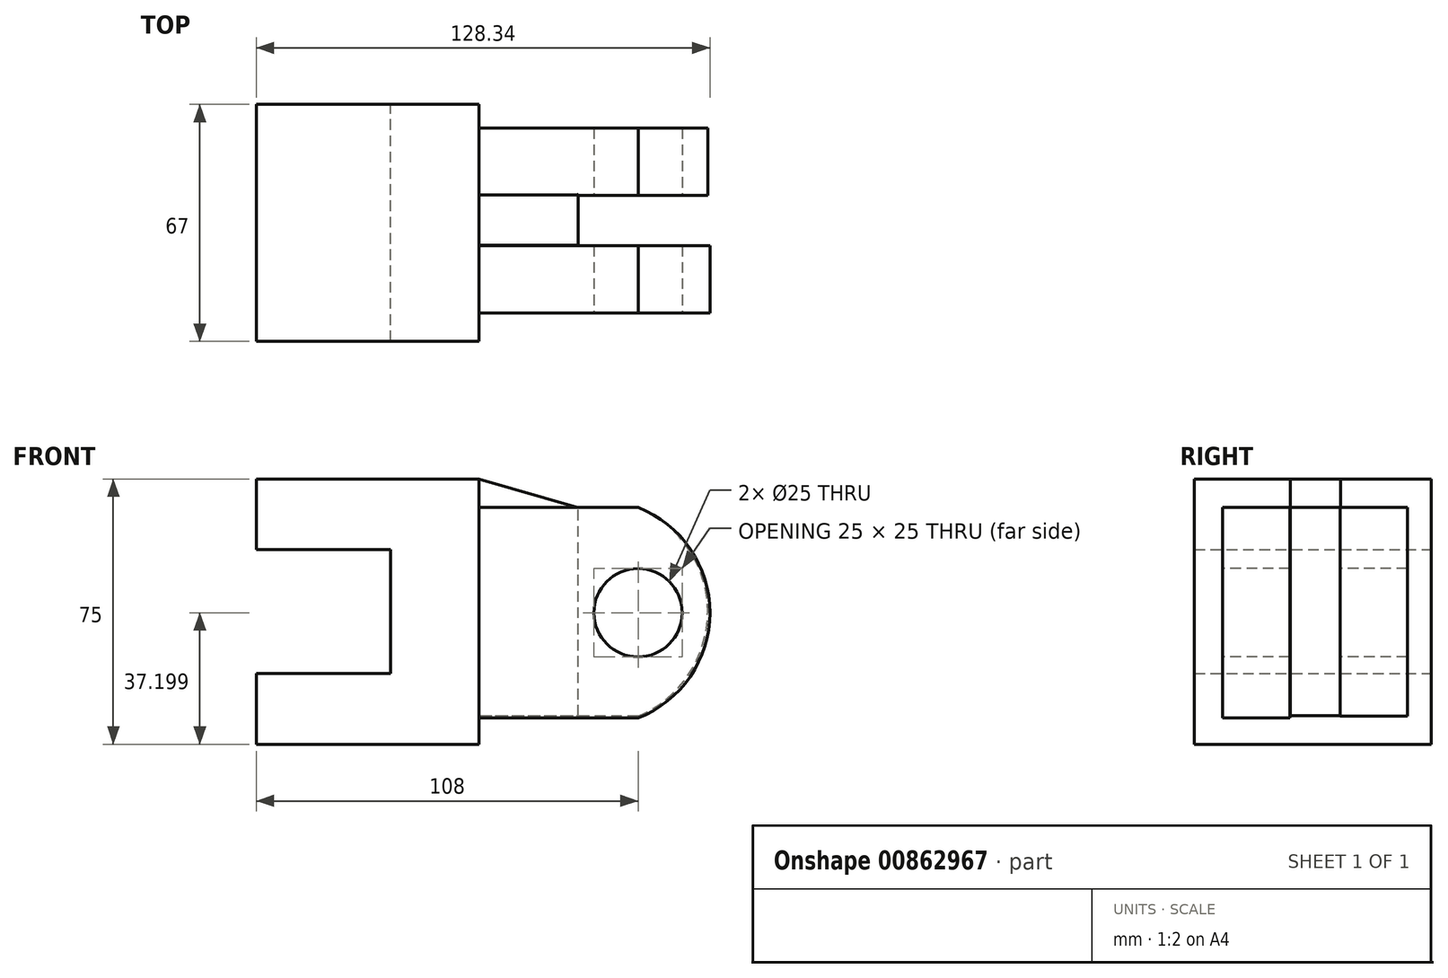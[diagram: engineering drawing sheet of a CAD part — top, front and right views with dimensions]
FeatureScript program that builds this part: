
annotation { "Feature Type Name" : "Feature", "Feature Type Description" : "" }
export const myFeature = defineFeature(function(context is Context, id is Id, definition is map)
    precondition{}
    {
        {
            var Q0;
            Q0=qCreatedBy(makeId("Front.planeOp"),FACE);
            var sketch = newSketch(context, id + "F0", { "sketchPlane" : qUnion([Q0])});
            skLineSegment(sketch, "E0", {"start": v(0, 0) * mm, "end": v(63, 0) * mm});
            skLineSegment(sketch, "E1", {"start": v(0, 0) * mm, "end": v(0, 20) * mm});
            skLineSegment(sketch, "E2", {"start": v(0, 20) * mm, "end": v(38, 20) * mm});
            skLineSegment(sketch, "E3", {"start": v(38, 20) * mm, "end": v(38, 55) * mm});
            skLineSegment(sketch, "E4", {"start": v(0, 55) * mm, "end": v(38, 55) * mm});
            skLineSegment(sketch, "E5", {"start": v(0, 55) * mm, "end": v(0, 75) * mm});
            skLineSegment(sketch, "E6", {"start": v(0, 75) * mm, "end": v(63, 75) * mm});
            skLineSegment(sketch, "E7", {"start": v(63, 75) * mm, "end": v(63, 0) * mm});
            skSolve(sketch);
        }
        {
            var Q0;
            Q0=makeQuery(id+"F0.imprint","IMPRINT",FACE,{"disambiguationData":[TD([[makeQuery(id+"F0.imprint","IMPRINT",EDGE,{"derivedFrom":sQuery(id+"F0.wireOp",EDGE,"E0")}),1.0]])]});
            extrude(context, id + "F1", {"entities" : qUnion([Q0]), "depth" : 67 * mm, "offsetDistance" : 25 * mm});
        }
        {
            var Q0;
            Q0=makeQuery(id+"F1.opExtrude","SWEPT_FACE",FACE,{"disambiguationData":[OSD([sQuery(id+"F0.wireOp",EDGE,"E7")])]});
            var sketch = newSketch(context, id + "F2", { "sketchPlane" : qUnion([Q0])});
            skLineSegment(sketch, "E8", {"start": v(-59, 7.4) * mm, "end": v(-40, 7.4) * mm});
            skLineSegment(sketch, "E9", {"start": v(-59, 7.4) * mm, "end": v(-59, 67) * mm});
            skLineSegment(sketch, "E10", {"start": v(-59, 67) * mm, "end": v(-40, 67) * mm});
            skLineSegment(sketch, "E11", {"start": v(-40, 67) * mm, "end": v(-40, 7.4) * mm});
            skSolve(sketch);
        }
        {
            var Q0;
            Q0=makeQuery(id+"F2.imprint","IMPRINT",FACE,{"disambiguationData":[TD([[makeQuery(id+"F2.imprint","IMPRINT",EDGE,{"derivedFrom":sQuery(id+"F2.wireOp",EDGE,"E8")}),1.0]])]});
            extrude(context, id + "F3", {"entities" : qUnion([Q0]), "operationType" : NewBodyOperationType.ADD, "depth" : 45 * mm, "offsetDistance" : 25 * mm});
        }
        {
            var Q0;
            Q0=makeQuery(id+"F1.opExtrude","SWEPT_FACE",FACE,{"disambiguationData":[OSD([sQuery(id+"F0.wireOp",EDGE,"E7")])]});
            var sketch = newSketch(context, id + "F4", { "sketchPlane" : qUnion([Q0])});
            skLineSegment(sketch, "E12", {"start": v(-6.74, 67) * mm, "end": v(-25.74, 67) * mm});
            skLineSegment(sketch, "E13", {"start": v(-25.74, 67) * mm, "end": v(-25.74, 7.93) * mm});
            skLineSegment(sketch, "E14", {"start": v(-6.74, 7.93) * mm, "end": v(-25.74, 7.93) * mm});
            skLineSegment(sketch, "E15", {"start": v(-6.74, 7.93) * mm, "end": v(-6.74, 67) * mm});
            skSolve(sketch);
        }
        {
            var Q0;
            Q0=makeQuery(id+"F4.imprint","IMPRINT",FACE,{"disambiguationData":[TD([[makeQuery(id+"F4.imprint","IMPRINT",EDGE,{"derivedFrom":sQuery(id+"F4.wireOp",EDGE,"E12")}),1.0]])]});
            extrude(context, id + "F5", {"entities" : qUnion([Q0]), "operationType" : NewBodyOperationType.ADD, "depth" : 45 * mm, "offsetDistance" : 25 * mm});
        }
        {
            var Q0;
            Q0=makeQuery(id+"F3.opExtrude","SWEPT_FACE",FACE,{"disambiguationData":[OSD([sQuery(id+"F2.wireOp",EDGE,"E9")])]});
            var sketch = newSketch(context, id + "F6", { "sketchPlane" : qUnion([Q0])});
            skArc(sketch, "E16", {"start": v(108, 7.4) * mm, "mid": v(128.34, 37.2) * mm, "end": v(108, 67) * mm});
            skSolve(sketch);
        }
        {
            var Q0;
            Q0=makeQuery(id+"F6.imprint","IMPRINT",FACE,{"disambiguationData":[TD([[makeQuery(id+"F6.imprint","IMPRINT",EDGE,{"derivedFrom":sQuery(id+"F6.wireOp",EDGE,"E16")}),1.0]])]});
            extrude(context, id + "F7", {"entities" : qUnion([Q0]), "operationType" : NewBodyOperationType.ADD, "oppositeDirection" : true, "depth" : 19 * mm, "offsetDistance" : 25 * mm});
        }
        {
            var Q0;
            Q0=makeQuery(id+"F5.opExtrude","SWEPT_FACE",FACE,{"disambiguationData":[OSD([sQuery(id+"F4.wireOp",EDGE,"E15")])]});
            var sketch = newSketch(context, id + "F8", { "sketchPlane" : qUnion([Q0])});
            skArc(sketch, "E17", {"start": v(-108, 67) * mm, "mid": v(-127.69, 37.46) * mm, "end": v(-108, 7.93) * mm});
            skSolve(sketch);
        }
        {
            var Q0;
            Q0 = qSketchRegion(id + "F8", true);
            var Q1;
            Q1=makeQuery(id+"F8.imprint","IMPRINT",FACE,{"disambiguationData":[TD([[makeQuery(id+"F8.imprint","IMPRINT",EDGE,{"derivedFrom":sQuery(id+"F8.wireOp",EDGE,"E17")}),1.0]])]});
            extrude(context, id + "F9", {"entities" : qUnion([Q0, Q1]), "operationType" : NewBodyOperationType.ADD, "oppositeDirection" : true, "depth" : 19 * mm, "offsetDistance" : 25 * mm});
        }
        {
            var Q0;
            Q0=makeQuery(id+"F1.opExtrude","SWEPT_FACE",FACE,{"disambiguationData":[OSD([sQuery(id+"F0.wireOp",EDGE,"E6")])]});
            var sketch = newSketch(context, id + "F10", { "sketchPlane" : qUnion([Q0])});
            skLineSegment(sketch, "E18", {"start": v(63, -39.88) * mm, "end": v(91, -39.88) * mm});
            skLineSegment(sketch, "E19", {"start": v(63, -25.59) * mm, "end": v(91, -25.59) * mm});
            skLineSegment(sketch, "E20", {"start": v(91, -39.88) * mm, "end": v(91, -25.59) * mm});
            skLineSegment(sketch, "E21", {"start": v(63, -25.59) * mm, "end": v(63, -39.88) * mm});
            skSolve(sketch);
        }
        {
            var Q0;
            Q0=makeQuery(id+"F10.imprint","IMPRINT",FACE,{"disambiguationData":[TD([[makeQuery(id+"F10.imprint","IMPRINT",EDGE,{"derivedFrom":sQuery(id+"F10.wireOp",EDGE,"E18")}),1.0]])]});
            extrude(context, id + "F11", {"entities" : qUnion([Q0]), "operationType" : NewBodyOperationType.ADD, "oppositeDirection" : true, "depth" : 66.9 * mm, "offsetDistance" : 25 * mm});
        }
        {
            var Q0;
            Q0=makeQuery(id+"F11.opExtrude","SWEPT_FACE",FACE,{"disambiguationData":[OSD([sQuery(id+"F10.wireOp",EDGE,"E18")])]});
            var sketch = newSketch(context, id + "F12", { "sketchPlane" : qUnion([Q0])});
            skLineSegment(sketch, "E22", {"start": v(91, 66.94) * mm, "end": v(63, 75) * mm});
            skSolve(sketch);
        }
        {
            var Q0;
            {var subQ0=sQuery(id+"F12.wireOp",EDGE,"E22");Q0=makeQuery(id+"F12.imprint","IMPRINT",FACE,{"disambiguationData":[TD([[makeQuery(id+"F12.imprint","IMPRINT",EDGE,{"derivedFrom":subQ0}),-1.0]])]});}
            extrude(context, id + "F13", {"entities" : qUnion([Q0]), "operationType" : NewBodyOperationType.REMOVE, "oppositeDirection" : true, "depth" : 14.4 * mm, "offsetDistance" : 25 * mm});
        }
        {
            var Q0;
            {var subQ0=sQuery(id+"F2.wireOp",EDGE,"E9");Q0=makeQuery(id+"F7.boolean.opBoolean","MERGE",FACE,{"derivedFrom":[makeQuery(id+"F3.opExtrude","SWEPT_FACE",FACE,{"disambiguationData":[OSD([subQ0])]}),makeQuery(id+"F7.opExtrude","CAP_FACE",FACE,{"disambiguationData":[OSD([subQ0,sQuery(id+"F6.wireOp",EDGE,"E16")])],"isStart":true})]});}
            var sketch = newSketch(context, id + "F14", { "sketchPlane" : qUnion([Q0])});
            skCircle(sketch, "E23", {"center": v(108, 37.2) * mm, "radius": 12.5 * mm});
            skPoint(sketch, "E23.centerSnap0", {"position": v(128.34, 37.2) * mm});
            skSolve(sketch);
        }
        {
            var Q0;
            Q0=makeQuery(id+"F14.imprint","IMPRINT",FACE,{"disambiguationData":[TD([[makeQuery(id+"F14.imprint","IMPRINT",EDGE,{"derivedFrom":sQuery(id+"F14.wireOp",EDGE,"E23")}),1.0]])]});
            extrude(context, id + "F15", {"entities" : qUnion([Q0]), "operationType" : NewBodyOperationType.REMOVE, "oppositeDirection" : true, "depth" : 65.5 * mm, "offsetDistance" : 25 * mm});
        }
    });
